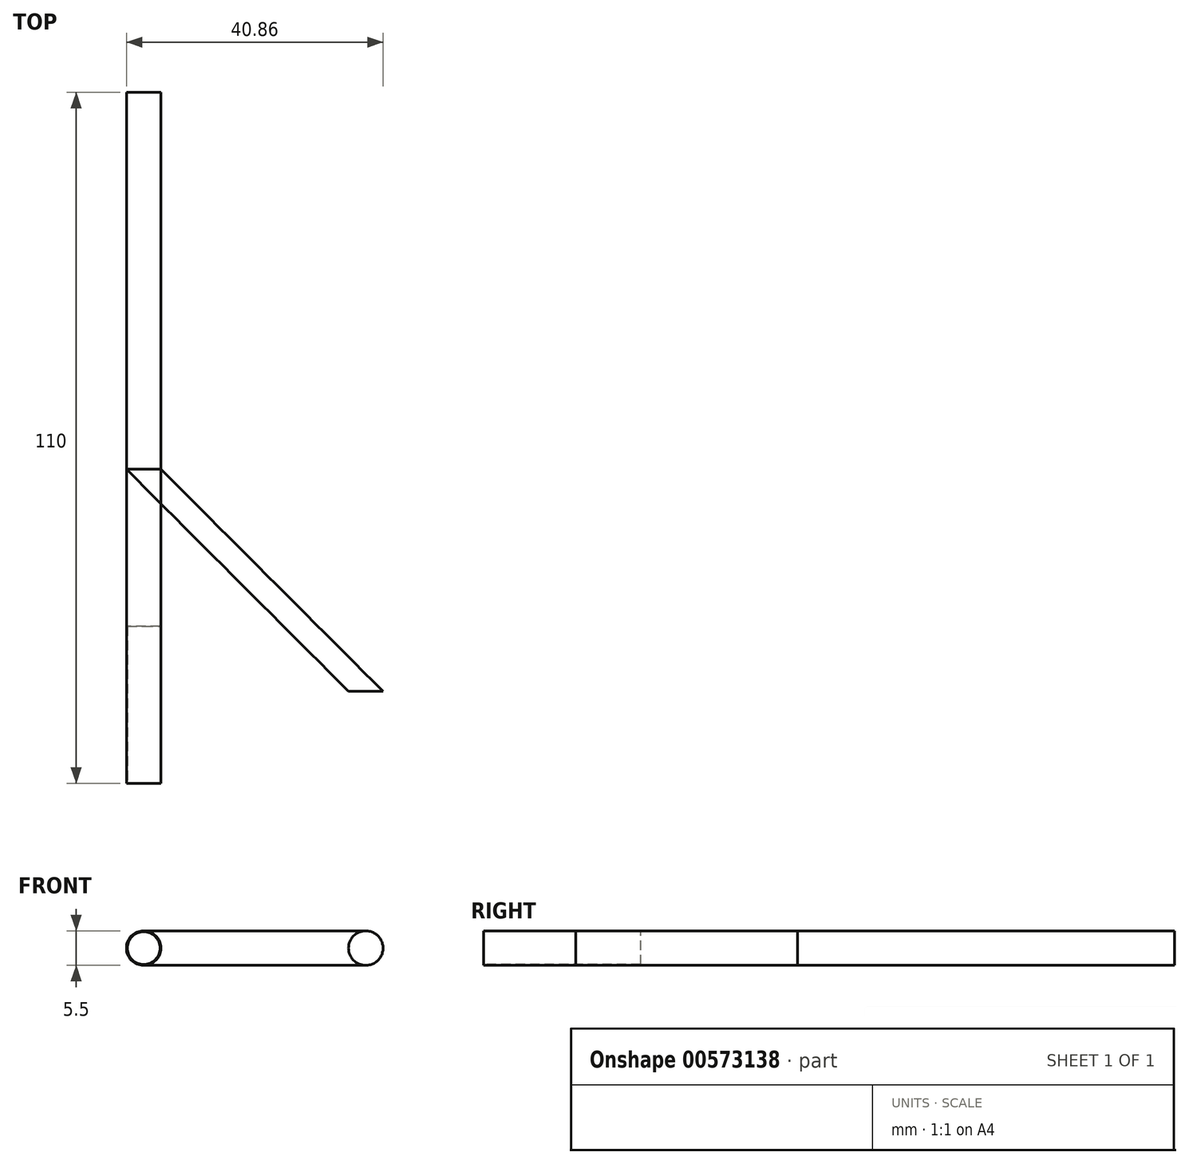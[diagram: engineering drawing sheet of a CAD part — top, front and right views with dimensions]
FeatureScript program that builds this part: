
annotation { "Feature Type Name" : "Feature", "Feature Type Description" : "" }
export const myFeature = defineFeature(function(context is Context, id is Id, definition is map)
    precondition{}
    {
        {
            var Q0;
            Q0=qCreatedBy(makeId("Top.planeOp"),FACE);
            var sketch = newSketch(context, id + "F0", { "sketchPlane" : qUnion([Q0])});
            skLineSegment(sketch, "E0", {"start": v(0, 0) * mm, "end": v(35.36, -35.36) * mm});
            skLineSegment(sketch, "E1", {"start": v(0, 0) * mm, "end": v(0, -50) * mm});
            skLineSegment(sketch, "E2", {"start": v(0, 0) * mm, "end": v(0, 60) * mm});
            skSolve(sketch);
        }
        {
            var Q0;
            Q0=qCreatedBy(makeId("Front.planeOp"),FACE);
            var sketch = newSketch(context, id + "F1", { "sketchPlane" : qUnion([Q0])});
            skCircle(sketch, "E3", {"center": v(0, 0) * mm, "radius": 2.75 * mm});
            skSolve(sketch);
        }
        {
            var Q0;
            Q0=makeQuery(id+"F1.imprint","IMPRINT",FACE,{"disambiguationData":[TD([[makeQuery(id+"F1.imprint","IMPRINT",EDGE,{"derivedFrom":sQuery(id+"F1.wireOp",EDGE,"E3")}),1.0]])]});
            var Q1;
            Q1=sQuery(id+"F0.wireOp",EDGE,"E1");
            sweep(context, id + "F2", {"profiles" : qUnion([Q0]), "path" : qUnion([Q1])});
        }
        {
            var Q0;
            Q0=makeQuery(id+"F2.opSweep","CAP_FACE",FACE,{"disambiguationData":[OSD([sQuery(id+"F0.wireOp",VERTEX,"E1.start"),sQuery(id+"F1.wireOp",EDGE,"E3")])],"isStart":true});
            var Q1;
            Q1=sQuery(id+"F0.wireOp",EDGE,"E0");
            sweep(context, id + "F3", {"profiles" : qUnion([Q0]), "path" : qUnion([Q1])});
        }
        {
            var Q0;
            Q0=makeQuery(id+"F1.imprint","IMPRINT",FACE,{"disambiguationData":[TD([[makeQuery(id+"F1.imprint","IMPRINT",EDGE,{"derivedFrom":sQuery(id+"F1.wireOp",EDGE,"E3")}),1.0]])]});
            var Q1;
            Q1=sQuery(id+"F0.wireOp",EDGE,"E2");
            sweep(context, id + "F4", {"profiles" : qUnion([Q0]), "path" : qUnion([Q1])});
        }
        {
            var Q0;
            Q0=makeQuery(id+"F2.opSweep","CAP_FACE",FACE,{"disambiguationData":[OSD([sQuery(id+"F0.wireOp",VERTEX,"E1.end"),sQuery(id+"F1.wireOp",EDGE,"E3")])],"isStart":false});
            var sketch = newSketch(context, id + "F5", { "sketchPlane" : qUnion([Q0])});
            skCircle(sketch, "E4", {"center": v(0, 0) * mm, "radius": 2.6 * mm});
            skSolve(sketch);
        }
        {
            var Q0;
            Q0=makeQuery(id+"F5.imprint","IMPRINT",FACE,{"disambiguationData":[TD([[makeQuery(id+"F5.imprint","IMPRINT",EDGE,{"derivedFrom":sQuery(id+"F5.wireOp",EDGE,"E4")}),1.0]])]});
            extrude(context, id + "F6", {"entities" : qUnion([Q0]), "oppositeDirection" : true, "depth" : 25 * mm, "offsetDistance" : 25 * mm});
        }
        {
            var Q0;
            Q0=makeQuery(id+"F3.opSweep","CAP_FACE",FACE,{"disambiguationData":[OSD([sQuery(id+"F0.wireOp",VERTEX,"E0.end"),sQuery(id+"F0.wireOp",VERTEX,"E1.start"),sQuery(id+"F1.wireOp",EDGE,"E3")])],"isStart":false});
            var sketch = newSketch(context, id + "F7", { "sketchPlane" : qUnion([Q0])});
            skCircle(sketch, "E5", {"center": v(35.36, 0) * mm, "radius": 2.5 * mm});
            skSolve(sketch);
        }
        {
            var Q0;
            Q0=qCreatedBy(makeId("Top.planeOp"),FACE);
            var sketch = newSketch(context, id + "F8", { "sketchPlane" : qUnion([Q0])});
            skLineSegment(sketch, "E6", {"start": v(35.32, -35.35) * mm, "end": v(39.79, -39.54) * mm});
            skSolve(sketch);
        }
    });
